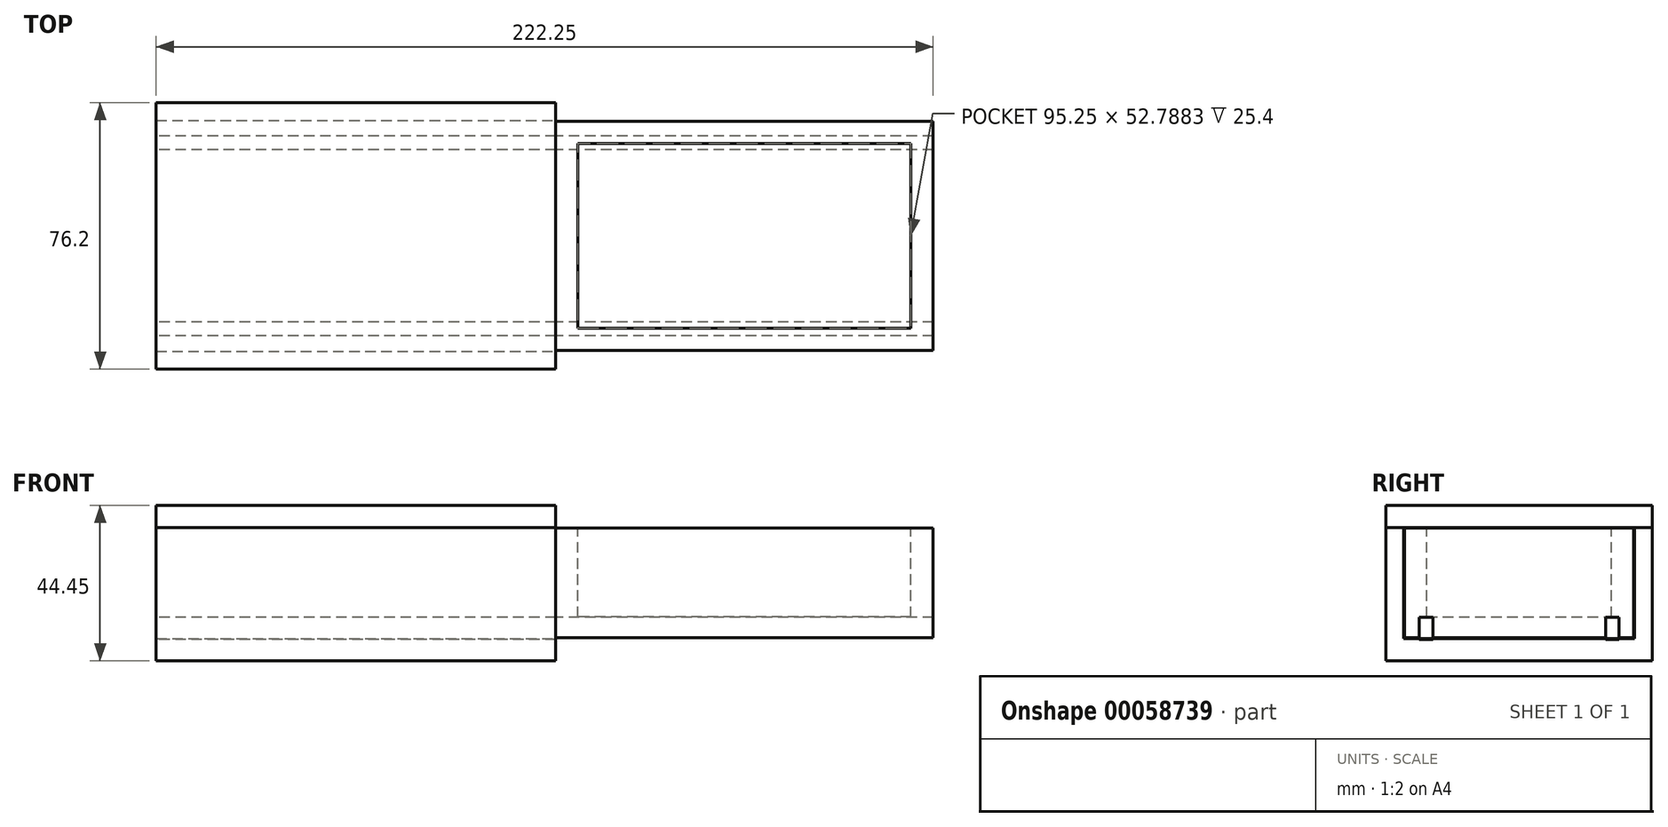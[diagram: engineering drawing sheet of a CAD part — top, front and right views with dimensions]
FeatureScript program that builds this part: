
annotation { "Feature Type Name" : "Feature", "Feature Type Description" : "" }
export const myFeature = defineFeature(function(context is Context, id is Id, definition is map)
    precondition{}
    {
        {
            var Q0;
            Q0=qCreatedBy(makeId("Top.planeOp"),FACE);
            var sketch = newSketch(context, id + "F0", { "sketchPlane" : qUnion([Q0])});
            skLineSegment(sketch, "E0.rect.bottom", {"start": v(-57.15, 38.1) * mm, "end": v(57.15, 38.1) * mm});
            skLineSegment(sketch, "E0.rect.top", {"start": v(-57.15, -38.1) * mm, "end": v(57.15, -38.1) * mm});
            skLineSegment(sketch, "E0.rect.left", {"start": v(-57.15, 38.1) * mm, "end": v(-57.15, -38.1) * mm});
            skLineSegment(sketch, "E0.rect.right", {"start": v(57.15, 38.1) * mm, "end": v(57.15, -38.1) * mm});
            skPoint(sketch, "E0.rect.middle", {"position": v(0, 0) * mm});
            skSolve(sketch);
        }
        {
            var Q0;
            Q0=makeQuery(id+"F0.imprint","IMPRINT",FACE,{"disambiguationData":[TD([[makeQuery(id+"F0.imprint","IMPRINT",EDGE,{"derivedFrom":sQuery(id+"F0.wireOp",EDGE,"E0.rect.bottom")}),-1.0]])]});
            extrude(context, id + "F1", {"entities" : qUnion([Q0]), "depth" : 6.35 * mm});
        }
        {
            var Q0;
            Q0=makeQuery(id+"F1.opExtrude","SWEPT_FACE",FACE,{"disambiguationData":[OSD([sQuery(id+"F0.wireOp",EDGE,"E0.rect.left")])]});
            var sketch = newSketch(context, id + "F2", { "sketchPlane" : qUnion([Q0])});
            skLineSegment(sketch, "E1.rect.bottom", {"start": v(-24.7, 12.45) * mm, "end": v(-28.6, 12.45) * mm});
            skLineSegment(sketch, "E1.rect.top", {"start": v(-24.7, 6.1) * mm, "end": v(-28.6, 6.1) * mm});
            skLineSegment(sketch, "E1.rect.left", {"start": v(-24.7, 12.45) * mm, "end": v(-24.7, 6.1) * mm});
            skLineSegment(sketch, "E1.rect.right", {"start": v(-28.6, 12.45) * mm, "end": v(-28.6, 6.1) * mm});
            skPoint(sketch, "E1.rect.middle", {"position": v(-26.65, 9.28) * mm});
            skLineSegment(sketch, "E2", {"start": v(0, 6.35) * mm, "end": v(0, 31.75) * mm, "construction": true});
            skPoint(sketch, "E3.MirrorP", {"position": v(26.65, 9.28) * mm});
            skLineSegment(sketch, "E4.MirrorCS", {"start": v(24.7, 12.45) * mm, "end": v(28.6, 12.45) * mm});
            skLineSegment(sketch, "E5.MirrorCS", {"start": v(24.7, 6.1) * mm, "end": v(28.6, 6.1) * mm});
            skLineSegment(sketch, "E6.MirrorCS", {"start": v(24.7, 12.45) * mm, "end": v(24.7, 6.1) * mm});
            skLineSegment(sketch, "E7.MirrorCS", {"start": v(28.6, 12.45) * mm, "end": v(28.6, 6.1) * mm});
            skSolve(sketch);
        }
        {
            var Q0;
            Q0 = qSketchRegion(id + "F2", true);
            extrude(context, id + "F3", {"entities" : qUnion([Q0]), "oppositeDirection" : true, "depth" : 114.3 * mm});
        }
        {
            var Q0;
            Q0=makeQuery(id+"F1.opExtrude","CAP_FACE",FACE,{"disambiguationData":[OSD([sQuery(id+"F0.wireOp",EDGE,"E0.rect.bottom"),sQuery(id+"F0.wireOp",EDGE,"E0.rect.top"),sQuery(id+"F0.wireOp",EDGE,"E0.rect.left"),sQuery(id+"F0.wireOp",EDGE,"E0.rect.right")])],"isStart":false});
            var sketch = newSketch(context, id + "F4", { "sketchPlane" : qUnion([Q0])});
            skLineSegment(sketch, "E8.bottom", {"start": v(-57.15, 38.1) * mm, "end": v(57.15, 38.1) * mm, "construction": true});
            skLineSegment(sketch, "E8.top", {"start": v(-57.15, 33.02) * mm, "end": v(57.15, 33.02) * mm});
            skLineSegment(sketch, "E8.left", {"start": v(-57.15, 38.1) * mm, "end": v(-57.15, 33.02) * mm});
            skLineSegment(sketch, "E8.right", {"start": v(57.15, 38.1) * mm, "end": v(57.15, 33.02) * mm});
            skLineSegment(sketch, "E9", {"start": v(57.15, 0) * mm, "end": v(-57.15, 0) * mm, "construction": true});
            skLineSegment(sketch, "E10.MirrorCS", {"start": v(57.15, -38.1) * mm, "end": v(57.15, -33.02) * mm});
            skLineSegment(sketch, "E11.MirrorCS", {"start": v(-57.15, -38.1) * mm, "end": v(-57.15, -33.02) * mm});
            skLineSegment(sketch, "E12.MirrorCS", {"start": v(-57.15, -33.02) * mm, "end": v(57.15, -33.02) * mm});
            skLineSegment(sketch, "E13.MirrorCS", {"start": v(-57.15, -38.1) * mm, "end": v(57.15, -38.1) * mm, "construction": true});
            skSolve(sketch);
        }
        {
            var Q0;
            Q0=makeQuery(id+"F4.imprint","IMPRINT",FACE,{"disambiguationData":[TD([[makeQuery(id+"F4.imprint","IMPRINT",EDGE,{"derivedFrom":sQuery(id+"F4.wireOp",EDGE,"E8.top")}),1.0]])]});
            var Q1;
            Q1=makeQuery(id+"F4.imprint","IMPRINT",FACE,{"disambiguationData":[TD([[makeQuery(id+"F4.imprint","IMPRINT",EDGE,{"derivedFrom":sQuery(id+"F4.wireOp",EDGE,"E10.MirrorCS")}),-1.0]])]});
            extrude(context, id + "F5", {"entities" : qUnion([Q0, Q1]), "operationType" : NewBodyOperationType.ADD, "depth" : 31.75 * mm});
        }
        {
            var Q0;
            Q0=makeQuery(id+"F3.opExtrude","CAP_FACE",FACE,{"disambiguationData":[OSD([sQuery(id+"F2.wireOp",EDGE,"E4.MirrorCS"),sQuery(id+"F2.wireOp",EDGE,"E5.MirrorCS"),sQuery(id+"F2.wireOp",EDGE,"E6.MirrorCS"),sQuery(id+"F2.wireOp",EDGE,"E7.MirrorCS")])],"isStart":false});
            var sketch = newSketch(context, id + "F6", { "sketchPlane" : qUnion([Q0])});
            skLineSegment(sketch, "E14.bottom", {"start": v(-32.77, 6.62) * mm, "end": v(32.72, 6.62) * mm});
            skLineSegment(sketch, "E14.top", {"start": v(-32.77, 37.94) * mm, "end": v(32.72, 37.94) * mm});
            skLineSegment(sketch, "E14.left", {"start": v(-32.77, 6.62) * mm, "end": v(-32.77, 37.94) * mm});
            skLineSegment(sketch, "E14.right", {"start": v(32.72, 6.62) * mm, "end": v(32.72, 37.94) * mm});
            skSolve(sketch);
        }
        {
            var Q0;
            Q0 = qSketchRegion(id + "F6", true);
            extrude(context, id + "F7", {"entities" : qUnion([Q0]), "depth" : 107.95 * mm});
        }
        {
            var Q0;
            Q0=makeQuery(id+"F3.opExtrude","CAP_FACE",FACE,{"disambiguationData":[OSD([sQuery(id+"F2.wireOp",EDGE,"E4.MirrorCS"),sQuery(id+"F2.wireOp",EDGE,"E5.MirrorCS"),sQuery(id+"F2.wireOp",EDGE,"E6.MirrorCS"),sQuery(id+"F2.wireOp",EDGE,"E7.MirrorCS")])],"isStart":false});
            var Q1;
            Q1=makeQuery(id+"F3.opExtrude","CAP_FACE",FACE,{"disambiguationData":[OSD([sQuery(id+"F2.wireOp",EDGE,"E1.rect.bottom"),sQuery(id+"F2.wireOp",EDGE,"E1.rect.top"),sQuery(id+"F2.wireOp",EDGE,"E1.rect.left"),sQuery(id+"F2.wireOp",EDGE,"E1.rect.right")])],"isStart":false});
            extrude(context, id + "F8", {"entities" : qUnion([Q0, Q1]), "operationType" : NewBodyOperationType.REMOVE, "depth" : 139.7 * mm});
        }
        {
            var Q0;
            Q0=makeQuery(id+"F7.opExtrude","SWEPT_FACE",FACE,{"disambiguationData":[OSD([sQuery(id+"F6.wireOp",EDGE,"E14.top")])]});
            var sketch = newSketch(context, id + "F9", { "sketchPlane" : qUnion([Q0])});
            skLineSegment(sketch, "E15", {"start": v(165.1, -32.77) * mm, "end": v(158.75, -32.77) * mm, "construction": true});
            skLineSegment(sketch, "E16", {"start": v(158.75, -32.77) * mm, "end": v(158.75, -26.42) * mm, "construction": true});
            skLineSegment(sketch, "E17", {"start": v(57.15, 32.72) * mm, "end": v(63.5, 32.72) * mm, "construction": true});
            skLineSegment(sketch, "E18", {"start": v(63.5, 32.72) * mm, "end": v(63.5, 26.37) * mm, "construction": true});
            skLineSegment(sketch, "E19.bottom", {"start": v(158.75, -26.42) * mm, "end": v(63.5, -26.42) * mm});
            skLineSegment(sketch, "E19.top", {"start": v(158.75, 26.37) * mm, "end": v(63.5, 26.37) * mm});
            skLineSegment(sketch, "E19.left", {"start": v(158.75, -26.42) * mm, "end": v(158.75, 26.37) * mm});
            skLineSegment(sketch, "E19.right", {"start": v(63.5, -26.42) * mm, "end": v(63.5, 26.37) * mm});
            skSolve(sketch);
        }
        {
            var Q0;
            Q0=makeQuery(id+"F5.opExtrude","CAP_FACE",FACE,{"disambiguationData":[OSD([sQuery(id+"F0.wireOp",EDGE,"E0.rect.bottom"),sQuery(id+"F4.wireOp",EDGE,"E8.top"),sQuery(id+"F4.wireOp",EDGE,"E8.left"),sQuery(id+"F4.wireOp",EDGE,"E8.right")])],"isStart":false});
            var sketch = newSketch(context, id + "F10", { "sketchPlane" : qUnion([Q0])});
            skLineSegment(sketch, "E20.rect.bottom", {"start": v(-57.15, -38.1) * mm, "end": v(57.15, -38.1) * mm});
            skLineSegment(sketch, "E20.rect.top", {"start": v(-57.15, 38.1) * mm, "end": v(57.15, 38.1) * mm});
            skLineSegment(sketch, "E20.rect.left", {"start": v(-57.15, -38.1) * mm, "end": v(-57.15, 38.1) * mm});
            skLineSegment(sketch, "E20.rect.right", {"start": v(57.15, -38.1) * mm, "end": v(57.15, 38.1) * mm});
            skPoint(sketch, "E20.rect.middle", {"position": v(0, 0) * mm});
            skSolve(sketch);
        }
        {
            var Q0;
            Q0=makeQuery(id+"F9.imprint","IMPRINT",FACE,{"disambiguationData":[TD([[makeQuery(id+"F9.imprint","IMPRINT",EDGE,{"derivedFrom":sQuery(id+"F9.wireOp",EDGE,"E19.bottom")}),-1.0]])]});
            extrude(context, id + "F11", {"entities" : qUnion([Q0]), "operationType" : NewBodyOperationType.REMOVE, "oppositeDirection" : true, "depth" : 25.4 * mm});
        }
        {
            var Q0;
            Q0 = qSketchRegion(id + "F10", true);
            extrude(context, id + "F12", {"entities" : qUnion([Q0]), "depth" : 6.35 * mm});
        }
    });
